# Revit family: Grinder_Pump-Horizontal-Zoeller-820_Series (1)
name_source: partatom
category: Mechanical Equipment
units: mm (PartAtom-declared; Revit-internal decimal feet)

## family parameters
Always vertical = No
Cut with Voids When Loaded = No
OmniClass Number = 23.60.30.21
OmniClass Title = Pumps
Part Type = Normal
Room Calculation Point = No
Round Connector Dimension = Use Radius
Shared = Yes
Work Plane-Based = Yes

## types (1)
- E820 - E820/230V/1Ph/60
    Adapter = Cast Iron
    Amps = 14 A
    Apparent Load = 3151 VA
    Assembly Code = D2090
    Auto On/Off Points = Variable level float switch, customer sets
    Cap = Cast Iron
    Cooling = Oil filled
    Cord Length = 240"
    Cord Type = SOW or SOOW multi-wire neoprene
    Cutter = Type 440C stainless steel hardened to a Rockwell C55-60
    Default Elevation = 0"
    Description = Horizontal Grinder Single Seal Pump With Integral Control.
    Discharge Diameter = 1 1/4"
    Discharge Radius = 5/8"
    Flow @ 5' = 46 GPM
    Hardware = Stainless Steel
    Height = 18 5/8"
    Hertz = 60
    Impeller = Engineered plastic
    Impeller Type = Vortex
    Installation Type = Floor Mounted
    Insulation = Class B
    Length = 8"
    Lower Bearing = Ball bearing
    Manufacturer = Zoeller
    Material = Cast Iron-Zoeller-Powder Coated Epoxy
    Max. Head = 1284"
    Max. Operating Temp. = 130°F (54°C)
    Mechanical Seals = Carbon/Ceramic
    Model = E820
    Motor = 2 HP
    Motor Housing = Cast Iron
    Motor Protection = Auto reset thermal overload
    Motor Shaft = Stainless Steel
    Nominal Height = 5"
    O-Ring Seals = Neoprene
    Operation = Non-Automatic
    Phase = 1
    Price = Prices may vary. Please consult Manufacturer Representative for most up-to-date price list.
    Pump Housing = Cast Iron
    RPM = 3450
    Shipping Weight = 88 lbs.
    Type = Capacitor Start/Run
    URL = http://www.zoellerengprod.com
    Upper Bearing = Ball Bearing
    Voltage = 230 V
    Warranty Information = 36 Months (Limited)
    Waste Connection = Yes
    Width = 11 5/8"

## geometry (parser evidence)
native form markers: Sweep x2
no freeform markers — native parametric forms only
